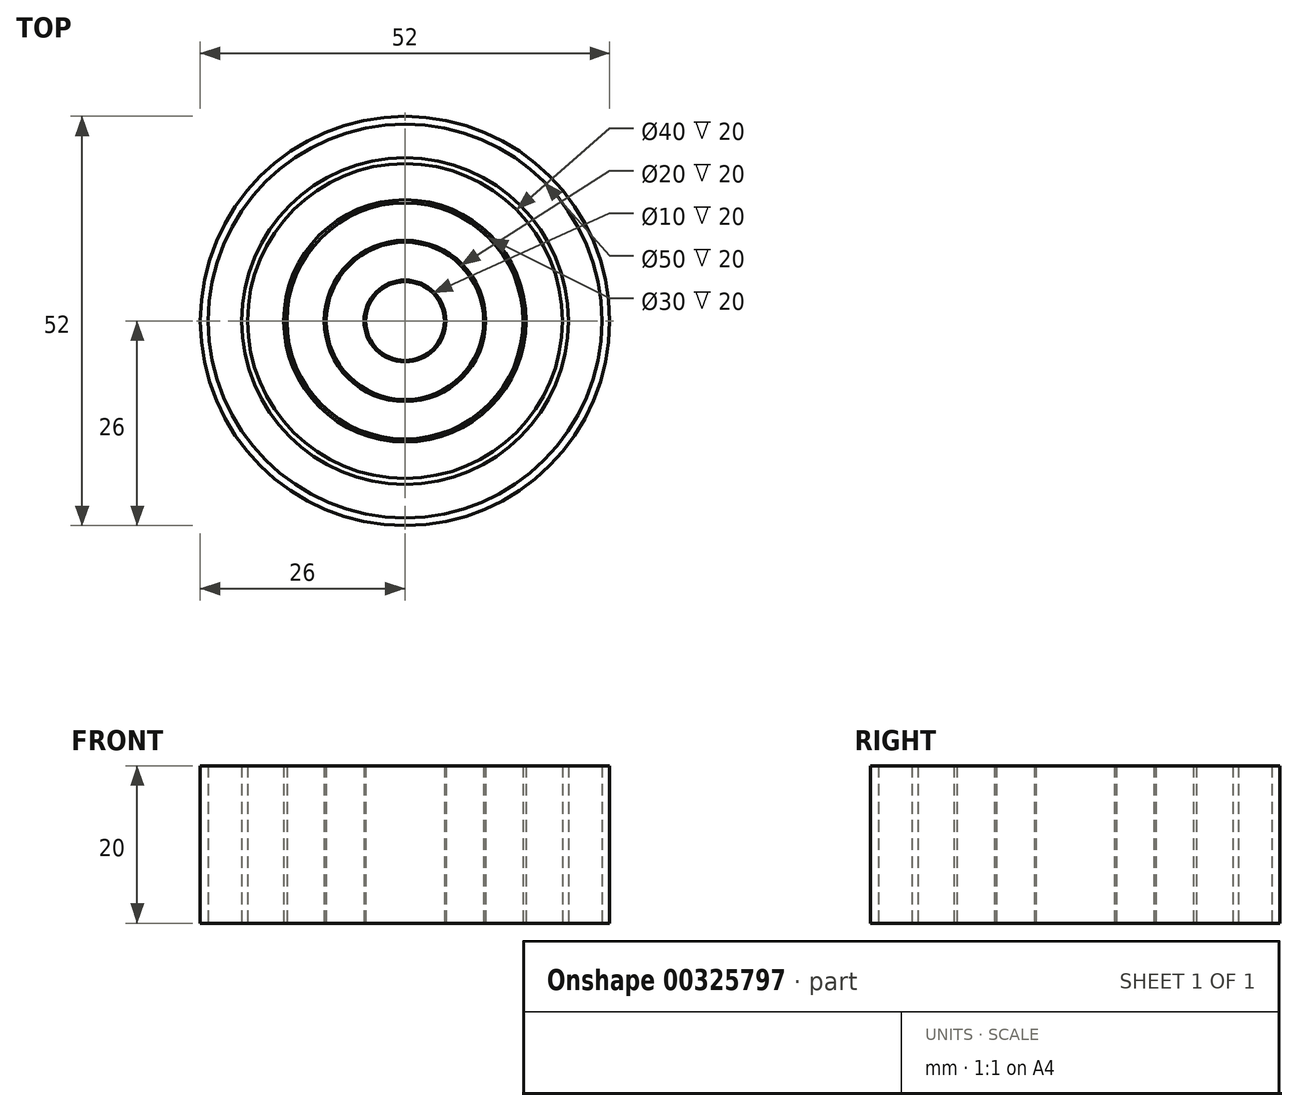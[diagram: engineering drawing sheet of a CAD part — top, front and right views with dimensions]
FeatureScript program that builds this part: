
annotation { "Feature Type Name" : "Feature", "Feature Type Description" : "" }
export const myFeature = defineFeature(function(context is Context, id is Id, definition is map)
    precondition{}
    {
        {
            var Q0;
            Q0=qCreatedBy(makeId("Top.planeOp"),FACE);
            var sketch = newSketch(context, id + "F0", { "sketchPlane" : qUnion([Q0])});
            skCircle(sketch, "E0", {"center": v(0, 0) * mm, "radius": 5 * mm});
            skCircle(sketch, "E1", {"center": v(0, 0) * mm, "radius": 5.2 * mm});
            skCircle(sketch, "E2", {"center": v(0, 0) * mm, "radius": 10 * mm});
            skCircle(sketch, "E3", {"center": v(0, 0) * mm, "radius": 10.25 * mm});
            skCircle(sketch, "E4", {"center": v(0, 0) * mm, "radius": 15 * mm});
            skCircle(sketch, "E5", {"center": v(0, 0) * mm, "radius": 15.4 * mm});
            skCircle(sketch, "E6", {"center": v(0, 0) * mm, "radius": 20 * mm});
            skCircle(sketch, "E7", {"center": v(0, 0) * mm, "radius": 20.75 * mm});
            skCircle(sketch, "E8", {"center": v(0, 0) * mm, "radius": 25 * mm});
            skCircle(sketch, "E9", {"center": v(0, 0) * mm, "radius": 26 * mm});
            skSolve(sketch);
        }
        {
            var Q0;
            Q0 = qSketchRegion(id + "F0", true);
            var Q1;
            Q1=makeQuery(id+"F0.imprint","IMPRINT",FACE,{"disambiguationData":[TD([[makeQuery(id+"F0.imprint","IMPRINT",EDGE,{"derivedFrom":sQuery(id+"F0.wireOp",EDGE,"E6")}),-1.0]])]});
            var Q2;
            Q2=makeQuery(id+"F0.imprint","IMPRINT",FACE,{"disambiguationData":[TD([[makeQuery(id+"F0.imprint","IMPRINT",EDGE,{"derivedFrom":sQuery(id+"F0.wireOp",EDGE,"E4")}),-1.0]])]});
            var Q3;
            Q3=makeQuery(id+"F0.imprint","IMPRINT",FACE,{"disambiguationData":[TD([[makeQuery(id+"F0.imprint","IMPRINT",EDGE,{"derivedFrom":sQuery(id+"F0.wireOp",EDGE,"E2")}),-1.0]])]});
            var Q4;
            Q4=makeQuery(id+"F0.imprint","IMPRINT",FACE,{"disambiguationData":[TD([[makeQuery(id+"F0.imprint","IMPRINT",EDGE,{"derivedFrom":sQuery(id+"F0.wireOp",EDGE,"E0")}),-1.0]])]});
            extrude(context, id + "F1", {"entities" : qUnion([Q0, Q1, Q2, Q3, Q4]), "depth" : 20 * mm});
        }
    });
